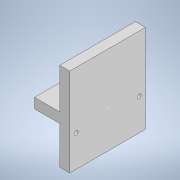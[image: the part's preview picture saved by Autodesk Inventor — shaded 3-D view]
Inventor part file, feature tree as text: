
AUTODESK INVENTOR PART (.ipt)
format: ipt  version: 2022.2 (Build 262287010, 287A)  size: 111,104 bytes
history: native  units: mm
features: sketch x3, extrude x1, hole x1
ambient origin geometry x8: Origin, YZ Plane, XZ Plane, XY Plane, X Axis, Y Axis, Z Axis, Center Point
bodies: Volumenkörper1 (feature_tree)
feature tree (5):
  extrude  "Extrusion1"  Depth=8.0mm
  sketch  "Skizze2"  dims[d2=20.0mm d3=8.0mm]
  hole  "Bohrung1"  [1 undecoded]
  sketch  "Skizze1"  dims[d0=70.0mm d1=8.0mm]
  sketch  "Skizze3"  dims[d4=40.0mm d5=60.0mm d6=0.0mm d7=50.0mm d8=45.0mm d9=3.4mm d10=6.0mm d11=6.5mm d12=3.4mm d13=14.3117mm d14=8.0mm d15=20.594885mm]
note: 1 required parameter value undecoded (feature->parameter linkage not recoverable at this tier; creation-order binding heuristic only, values carry confidence <= 0.55)
